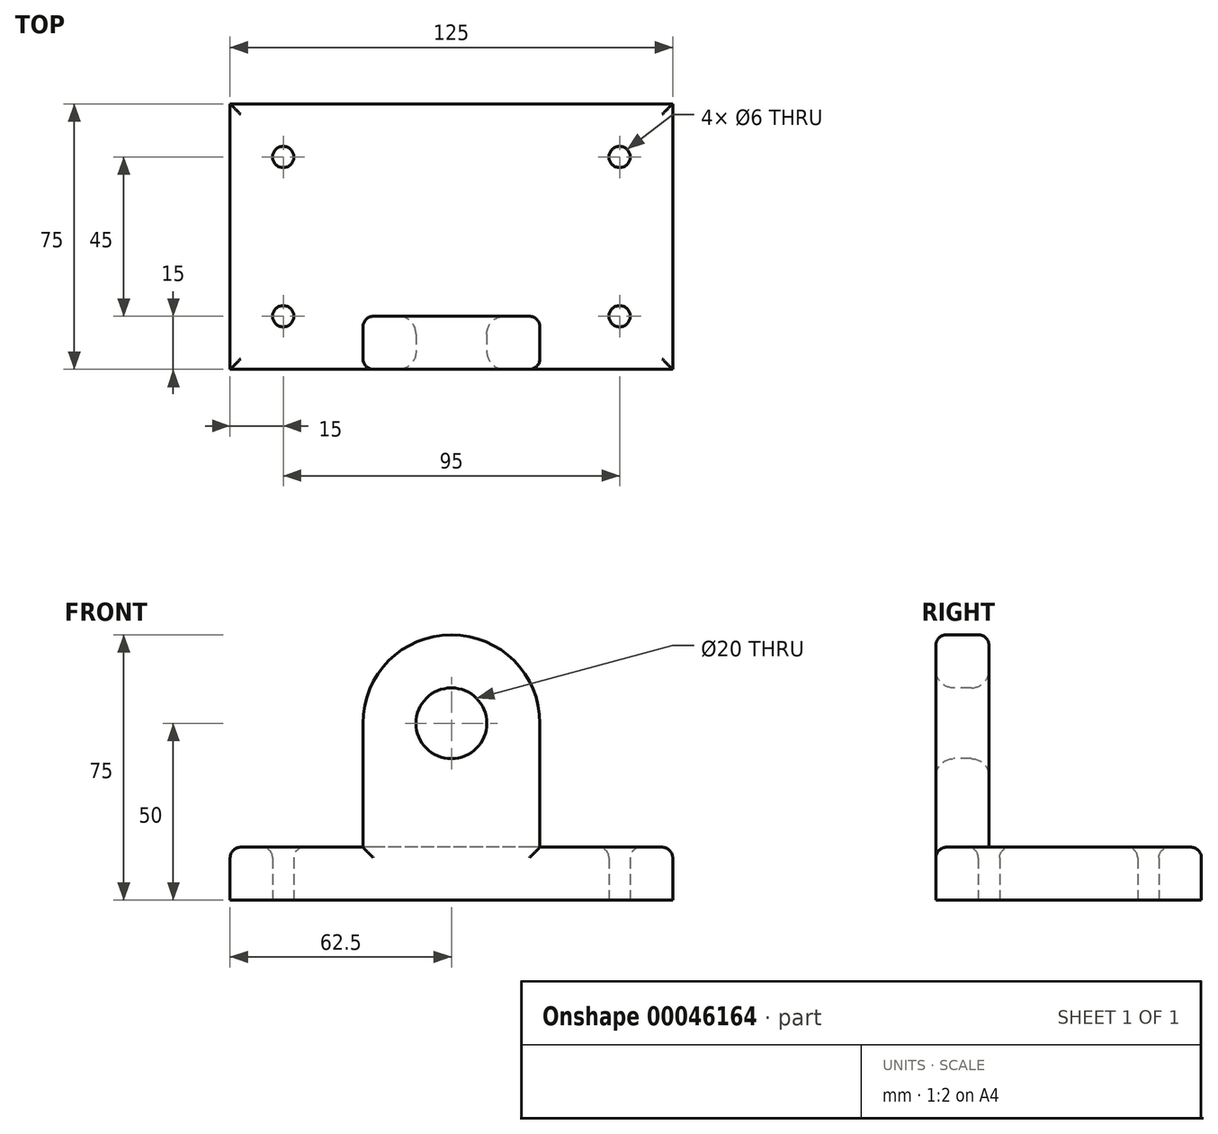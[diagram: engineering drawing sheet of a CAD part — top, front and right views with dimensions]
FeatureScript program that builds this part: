
annotation { "Feature Type Name" : "Feature", "Feature Type Description" : "" }
export const myFeature = defineFeature(function(context is Context, id is Id, definition is map)
    precondition{}
    {
        {
            var Q0;
            Q0=qCreatedBy(makeId("Top.planeOp"),FACE);
            var sketch = newSketch(context, id + "F0", { "sketchPlane" : qUnion([Q0])});
            skLineSegment(sketch, "E0.rect.bottom", {"start": v(62.5, 37.5) * mm, "end": v(-62.5, 37.5) * mm});
            skLineSegment(sketch, "E0.rect.top", {"start": v(62.5, -37.5) * mm, "end": v(-62.5, -37.5) * mm});
            skLineSegment(sketch, "E0.rect.left", {"start": v(62.5, 37.5) * mm, "end": v(62.5, -37.5) * mm});
            skLineSegment(sketch, "E0.rect.right", {"start": v(-62.5, 37.5) * mm, "end": v(-62.5, -37.5) * mm});
            skPoint(sketch, "E0.rect.middle", {"position": v(0, 0) * mm});
            skSolve(sketch);
        }
        {
            var Q0;
            Q0=makeQuery(id+"F0.imprint","IMPRINT",FACE,{"disambiguationData":[TD([[makeQuery(id+"F0.imprint","IMPRINT",EDGE,{"derivedFrom":sQuery(id+"F0.wireOp",EDGE,"E0.rect.bottom")}),1.0]])]});
            extrude(context, id + "F1", {"entities" : qUnion([Q0]), "depth" : 15 * mm});
        }
        {
            var Q0;
            Q0=makeQuery(id+"F1.opExtrude","SWEPT_FACE",FACE,{"disambiguationData":[OSD([sQuery(id+"F0.wireOp",EDGE,"E0.rect.top")])]});
            var sketch = newSketch(context, id + "F2", { "sketchPlane" : qUnion([Q0])});
            skLineSegment(sketch, "E1", {"start": v(0, 0) * mm, "end": v(0, 50) * mm, "construction": true});
            skCircle(sketch, "E2", {"center": v(0, 50) * mm, "radius": 25 * mm});
            skLineSegment(sketch, "E3", {"start": v(0, 50) * mm, "end": v(-25, 50) * mm});
            skLineSegment(sketch, "E4", {"start": v(0, 50) * mm, "end": v(25, 50) * mm});
            skLineSegment(sketch, "E5", {"start": v(-25, 50) * mm, "end": v(-25, 0) * mm});
            skLineSegment(sketch, "E6", {"start": v(25, 50) * mm, "end": v(25, 0) * mm});
            skLineSegment(sketch, "E7", {"start": v(-25, 0) * mm, "end": v(25, 0) * mm});
            skCircle(sketch, "E8", {"center": v(0, 50) * mm, "radius": 10 * mm});
            skSolve(sketch);
        }
        {
            var Q0;
            {var subQ1=sQuery(id+"F2.wireOp",EDGE,"E8");var subQ5=sQuery(id+"F2.wireOp",EDGE,"E3");var subQ6=makeQuery(id+"F2.imprint","INTERSECT",VERTEX,{"derivedFrom":[subQ5,subQ1]});Q0=makeQuery(id+"F2.imprint","IMPRINT",FACE,{"disambiguationData":[TD([[makeQuery(id+"F2.imprint","IMPRINT",EDGE,{"disambiguationData":[TD([[subQ6,1.0]])],"derivedFrom":subQ1}),-1.0]])]});}
            var Q1;
            {var subQ0=sQuery(id+"F2.wireOp",EDGE,"E8");var subQ3=sQuery(id+"F2.wireOp",EDGE,"E3");var subQ4=makeQuery(id+"F2.imprint","INTERSECT",VERTEX,{"derivedFrom":[subQ3,subQ0]});Q1=makeQuery(id+"F2.imprint","IMPRINT",FACE,{"disambiguationData":[TD([[makeQuery(id+"F2.imprint","IMPRINT",EDGE,{"disambiguationData":[TD([[subQ4,-1.0]])],"derivedFrom":subQ0}),-1.0]])]});}
            var Q2;
            {var subQ0=makeQuery(id+"F1.opExtrude","CAP_EDGE",EDGE,{"disambiguationData":[OSD([sQuery(id+"F0.wireOp",EDGE,"E0.rect.top")])],"isStart":false});var subQ3=sQuery(id+"F2.wireOp",EDGE,"E5");var subQ4=makeQuery(id+"F2.imprint","INTERSECT",VERTEX,{"derivedFrom":[subQ0,subQ3]});Q2=makeQuery(id+"F2.imprint","IMPRINT",FACE,{"disambiguationData":[TD([[makeQuery(id+"F2.imprint","IMPRINT",EDGE,{"disambiguationData":[TD([[subQ4,1.0]])],"derivedFrom":subQ0}),-1.0]])]});}
            extrude(context, id + "F3", {"entities" : qUnion([Q0, Q1, Q2]), "operationType" : NewBodyOperationType.ADD, "oppositeDirection" : true, "depth" : 15 * mm});
        }
        {
            var Q0;
            Q0=makeQuery(id+"F1.opExtrude","CAP_FACE",FACE,{"disambiguationData":[OSD([sQuery(id+"F0.wireOp",EDGE,"E0.rect.bottom"),sQuery(id+"F0.wireOp",EDGE,"E0.rect.top"),sQuery(id+"F0.wireOp",EDGE,"E0.rect.left"),sQuery(id+"F0.wireOp",EDGE,"E0.rect.right")])],"isStart":true});
            var sketch = newSketch(context, id + "F4", { "sketchPlane" : qUnion([Q0])});
            skLineSegment(sketch, "E9.rect.bottom", {"start": v(47.5, 22.5) * mm, "end": v(-47.5, 22.5) * mm, "construction": true});
            skLineSegment(sketch, "E9.rect.top", {"start": v(47.5, -22.5) * mm, "end": v(-47.5, -22.5) * mm, "construction": true});
            skLineSegment(sketch, "E9.rect.left", {"start": v(47.5, 22.5) * mm, "end": v(47.5, -22.5) * mm, "construction": true});
            skLineSegment(sketch, "E9.rect.right", {"start": v(-47.5, 22.5) * mm, "end": v(-47.5, -22.5) * mm, "construction": true});
            skPoint(sketch, "E9.rect.middle", {"position": v(0, 0) * mm});
            skCircle(sketch, "E10", {"center": v(-47.5, 22.5) * mm, "radius": 3 * mm});
            skCircle(sketch, "E11", {"center": v(47.5, 22.5) * mm, "radius": 3 * mm});
            skCircle(sketch, "E12", {"center": v(47.5, -22.5) * mm, "radius": 3 * mm});
            skCircle(sketch, "E13", {"center": v(-47.5, -22.5) * mm, "radius": 3 * mm});
            skSolve(sketch);
        }
        {
            var Q0;
            Q0 = qSketchRegion(id + "F4", true);
            extrude(context, id + "F5", {"entities" : qUnion([Q0]), "operationType" : NewBodyOperationType.REMOVE, "endBound" : BoundingType.THROUGH_ALL, "oppositeDirection" : true, "depth" : 25 * mm});
        }
        {
            var Q0;
            Q0=makeQuery(id+"F3.opExtrude","CAP_EDGE",EDGE,{"disambiguationData":[OSD([sQuery(id+"F2.wireOp",EDGE,"E2")])],"isStart":true});
            var Q1;
            Q1=makeQuery(id+"F3.opExtrude","CAP_EDGE",EDGE,{"disambiguationData":[OSD([sQuery(id+"F2.wireOp",EDGE,"E2")])],"isStart":false});
            var Q2;
            Q2=makeQuery(id+"F3.opExtrude","CAP_EDGE",EDGE,{"disambiguationData":[OSD([sQuery(id+"F2.wireOp",EDGE,"E6")])],"isStart":false});
            var Q3;
            Q3=makeQuery(id+"F3.opExtrude","CAP_EDGE",EDGE,{"disambiguationData":[OSD([sQuery(id+"F2.wireOp",EDGE,"E6")])],"isStart":true});
            var Q4;
            Q4=makeQuery(id+"F3.opExtrude","CAP_EDGE",EDGE,{"disambiguationData":[OSD([sQuery(id+"F2.wireOp",EDGE,"E5")])],"isStart":true});
            var Q5;
            {var subQ0=sQuery(id+"F0.wireOp",EDGE,"E0.rect.top");var subQ2=sQuery(id+"F0.wireOp",EDGE,"E0.rect.right");Q5=makeQuery(id+"F3.boolean.opBoolean","SPLIT",EDGE,{"disambiguationData":[TD([makeQuery(id+"F1.opExtrude","SWEPT_FACE",FACE,{"disambiguationData":[OSD([subQ2])]})])],"derivedFrom":makeQuery(id+"F1.opExtrude","CAP_EDGE",EDGE,{"disambiguationData":[OSD([subQ0])],"isStart":false})});}
            var Q6;
            Q6=makeQuery(id+"F1.opExtrude","CAP_EDGE",EDGE,{"disambiguationData":[OSD([sQuery(id+"F0.wireOp",EDGE,"E0.rect.right")])],"isStart":false});
            var Q7;
            Q7=makeQuery(id+"F1.opExtrude","CAP_EDGE",EDGE,{"disambiguationData":[OSD([sQuery(id+"F0.wireOp",EDGE,"E0.rect.bottom")])],"isStart":false});
            var Q8;
            Q8=makeQuery(id+"F1.opExtrude","CAP_EDGE",EDGE,{"disambiguationData":[OSD([sQuery(id+"F0.wireOp",EDGE,"E0.rect.left")])],"isStart":false});
            var Q9;
            {var subQ0=sQuery(id+"F0.wireOp",EDGE,"E0.rect.top");var subQ2=sQuery(id+"F0.wireOp",EDGE,"E0.rect.left");Q9=makeQuery(id+"F3.boolean.opBoolean","SPLIT",EDGE,{"disambiguationData":[TD([makeQuery(id+"F1.opExtrude","SWEPT_FACE",FACE,{"disambiguationData":[OSD([subQ2])]})])],"derivedFrom":makeQuery(id+"F1.opExtrude","CAP_EDGE",EDGE,{"disambiguationData":[OSD([subQ0])],"isStart":false})});}
            var Q10;
            Q10=makeQuery(id+"F3.opExtrude","SWEPT_EDGE",EDGE,{"disambiguationData":[OSD([sQuery(id+"F0.wireOp",EDGE,"E0.rect.top"),sQuery(id+"F2.wireOp",EDGE,"E6")])]});
            var Q11;
            Q11=makeQuery(id+"F3.opExtrude","SWEPT_EDGE",EDGE,{"disambiguationData":[OSD([sQuery(id+"F0.wireOp",EDGE,"E0.rect.top"),sQuery(id+"F2.wireOp",EDGE,"E5")])]});
            var Q12;
            Q12=makeQuery(id+"F3.opExtrude","CAP_EDGE",EDGE,{"disambiguationData":[OSD([sQuery(id+"F0.wireOp",EDGE,"E0.rect.top")])],"isStart":false});
            var Q13;
            Q13=makeQuery(id+"F5.boolean.opBoolean","INTERSECT",EDGE,{"derivedFrom":[makeQuery(id+"F1.opExtrude","CAP_FACE",FACE,{"disambiguationData":[OSD([sQuery(id+"F0.wireOp",EDGE,"E0.rect.bottom"),sQuery(id+"F0.wireOp",EDGE,"E0.rect.top"),sQuery(id+"F0.wireOp",EDGE,"E0.rect.left"),sQuery(id+"F0.wireOp",EDGE,"E0.rect.right")])],"isStart":false}),makeQuery(id+"F5.opExtrude","SWEPT_FACE",FACE,{"disambiguationData":[OSD([sQuery(id+"F4.wireOp",EDGE,"E13")])]})]});
            var Q14;
            Q14=makeQuery(id+"F5.boolean.opBoolean","INTERSECT",EDGE,{"derivedFrom":[makeQuery(id+"F1.opExtrude","CAP_FACE",FACE,{"disambiguationData":[OSD([sQuery(id+"F0.wireOp",EDGE,"E0.rect.bottom"),sQuery(id+"F0.wireOp",EDGE,"E0.rect.top"),sQuery(id+"F0.wireOp",EDGE,"E0.rect.left"),sQuery(id+"F0.wireOp",EDGE,"E0.rect.right")])],"isStart":false}),makeQuery(id+"F5.opExtrude","SWEPT_FACE",FACE,{"disambiguationData":[OSD([sQuery(id+"F4.wireOp",EDGE,"E10")])]})]});
            var Q15;
            Q15=makeQuery(id+"F5.boolean.opBoolean","INTERSECT",EDGE,{"derivedFrom":[makeQuery(id+"F1.opExtrude","CAP_FACE",FACE,{"disambiguationData":[OSD([sQuery(id+"F0.wireOp",EDGE,"E0.rect.bottom"),sQuery(id+"F0.wireOp",EDGE,"E0.rect.top"),sQuery(id+"F0.wireOp",EDGE,"E0.rect.left"),sQuery(id+"F0.wireOp",EDGE,"E0.rect.right")])],"isStart":false}),makeQuery(id+"F5.opExtrude","SWEPT_FACE",FACE,{"disambiguationData":[OSD([sQuery(id+"F4.wireOp",EDGE,"E11")])]})]});
            var Q16;
            Q16=makeQuery(id+"F5.boolean.opBoolean","INTERSECT",EDGE,{"derivedFrom":[makeQuery(id+"F1.opExtrude","CAP_FACE",FACE,{"disambiguationData":[OSD([sQuery(id+"F0.wireOp",EDGE,"E0.rect.bottom"),sQuery(id+"F0.wireOp",EDGE,"E0.rect.top"),sQuery(id+"F0.wireOp",EDGE,"E0.rect.left"),sQuery(id+"F0.wireOp",EDGE,"E0.rect.right")])],"isStart":false}),makeQuery(id+"F5.opExtrude","SWEPT_FACE",FACE,{"disambiguationData":[OSD([sQuery(id+"F4.wireOp",EDGE,"E12")])]})]});
            fillet(context, id + "F6", {"entities" : qUnion([Q0, Q1, Q2, Q3, Q4, Q5, Q6, Q7, Q8, Q9, Q10, Q11, Q12, Q13, Q14, Q15, Q16]), "radius" : 3 * mm, "tangentPropagation" : true, "allowEdgeOverflow" : false});
        }
        {
            var Q0;
            Q0=makeQuery(id+"F3.opExtrude","CAP_EDGE",EDGE,{"disambiguationData":[OSD([sQuery(id+"F2.wireOp",EDGE,"E8")])],"isStart":true});
            var Q1;
            Q1=makeQuery(id+"F3.opExtrude","CAP_EDGE",EDGE,{"disambiguationData":[OSD([sQuery(id+"F2.wireOp",EDGE,"E8")])],"isStart":false});
            fillet(context, id + "F7", {"entities" : qUnion([Q0, Q1]), "radius" : 5 * mm, "tangentPropagation" : true, "allowEdgeOverflow" : false});
        }
    });
